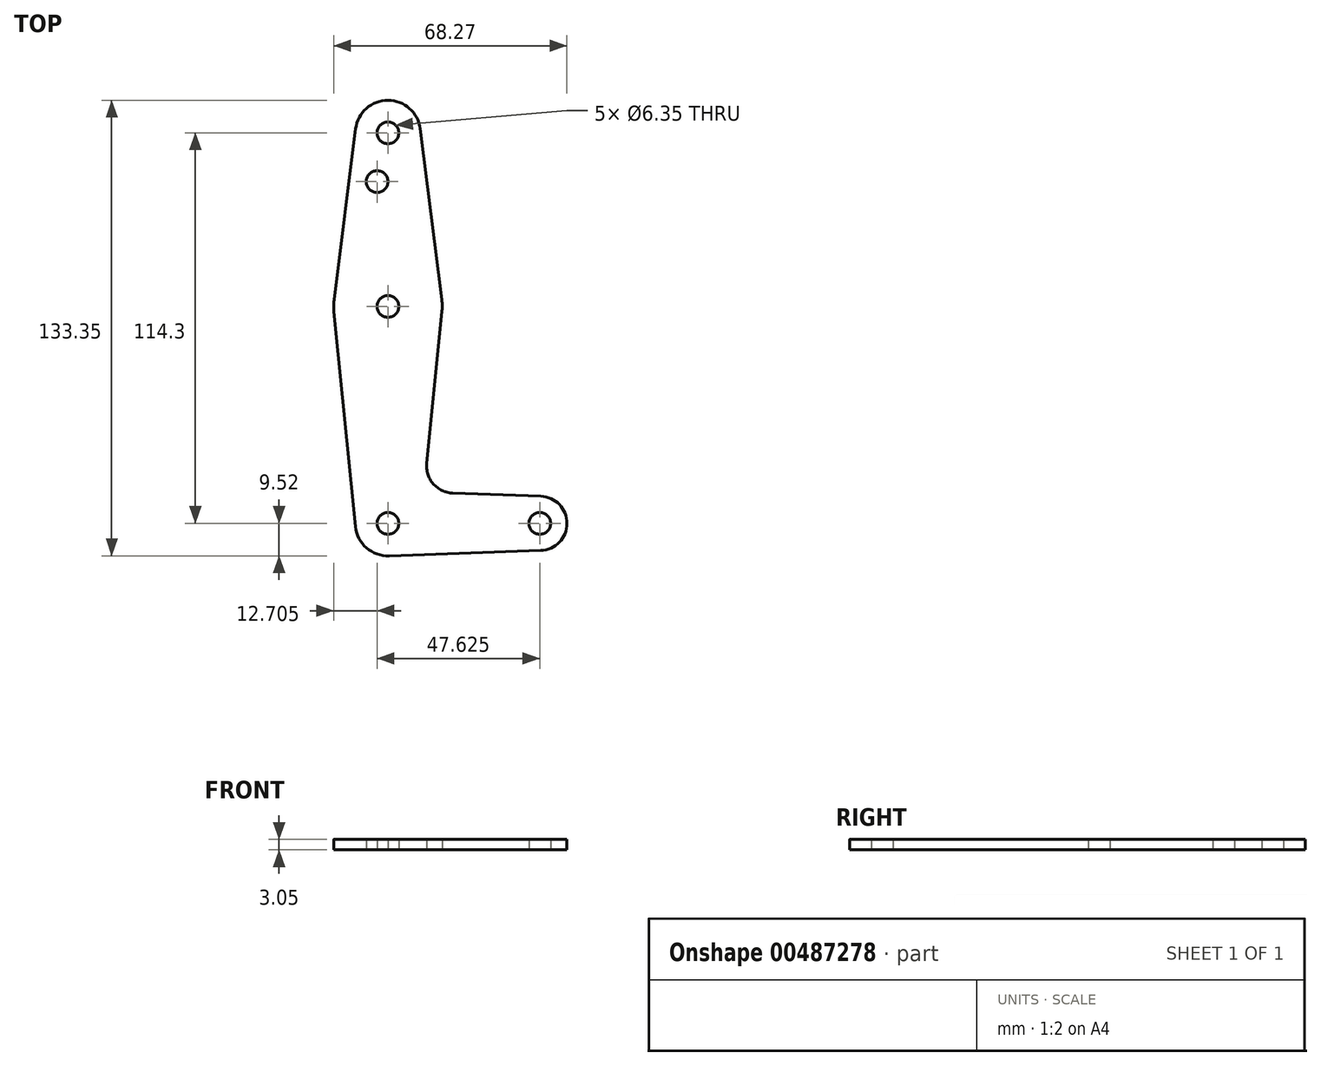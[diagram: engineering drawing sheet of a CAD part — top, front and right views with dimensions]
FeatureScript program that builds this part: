
annotation { "Feature Type Name" : "Feature", "Feature Type Description" : "" }
export const myFeature = defineFeature(function(context is Context, id is Id, definition is map)
    precondition{}
    {
        {
            var Q0;
            Q0=qCreatedBy(makeId("Top.planeOp"),FACE);
            var sketch = newSketch(context, id + "F0", { "sketchPlane" : qUnion([Q0])});
            skLineSegment(sketch, "E0", {"start": v(0, 0) * mm, "end": v(0, 114.3) * mm, "construction": true});
            skLineSegment(sketch, "E1", {"start": v(0, 0) * mm, "end": v(44.45, 0) * mm, "construction": true});
            skCircle(sketch, "E2", {"center": v(0, 114.3) * mm, "radius": 9.53 * mm});
            skCircle(sketch, "E3", {"center": v(0, 0) * mm, "radius": 9.53 * mm});
            skCircle(sketch, "E4", {"center": v(44.45, 0) * mm, "radius": 7.94 * mm});
            skCircle(sketch, "E5", {"center": v(0, 63.5) * mm, "radius": 15.88 * mm});
            skLineSegment(sketch, "E6", {"start": v(9.45, 115.5) * mm, "end": v(15.75, 65.48) * mm});
            skLineSegment(sketch, "E7", {"start": v(-9.45, 115.5) * mm, "end": v(-15.75, 65.48) * mm});
            skLineSegment(sketch, "E8", {"start": v(15.8, 61.91) * mm, "end": v(11.34, 17.6) * mm});
            skLineSegment(sketch, "E9", {"start": v(-9.48, -0.95) * mm, "end": v(-15.8, 61.91) * mm});
            skLineSegment(sketch, "E10", {"start": v(18.97, 8.85) * mm, "end": v(44.73, 7.93) * mm});
            skLineSegment(sketch, "E11", {"start": v(0.34, -9.52) * mm, "end": v(44.73, -7.93) * mm});
            skCircle(sketch, "E12", {"center": v(0, 114.3) * mm, "radius": 3.18 * mm});
            skCircle(sketch, "E13", {"center": v(0, 63.5) * mm, "radius": 3.18 * mm});
            skCircle(sketch, "E14", {"center": v(0, 0) * mm, "radius": 3.18 * mm});
            skCircle(sketch, "E15", {"center": v(44.45, 0) * mm, "radius": 3.18 * mm});
            skCircle(sketch, "E16", {"center": v(-3.18, 100.03) * mm, "radius": 3.18 * mm});
            skArc(sketch, "E17.filletArc", {"start": v(11.34, 17.6) * mm, "mid": v(13.26, 11.57) * mm, "end": v(18.97, 8.85) * mm});
            skSolve(sketch);
        }
        {
            var Q0;
            Q0 = qSketchRegion(id + "F0", true);
            extrude(context, id + "F1", {"entities" : qUnion([Q0]), "depth" : 3.05 * mm});
        }
    });
